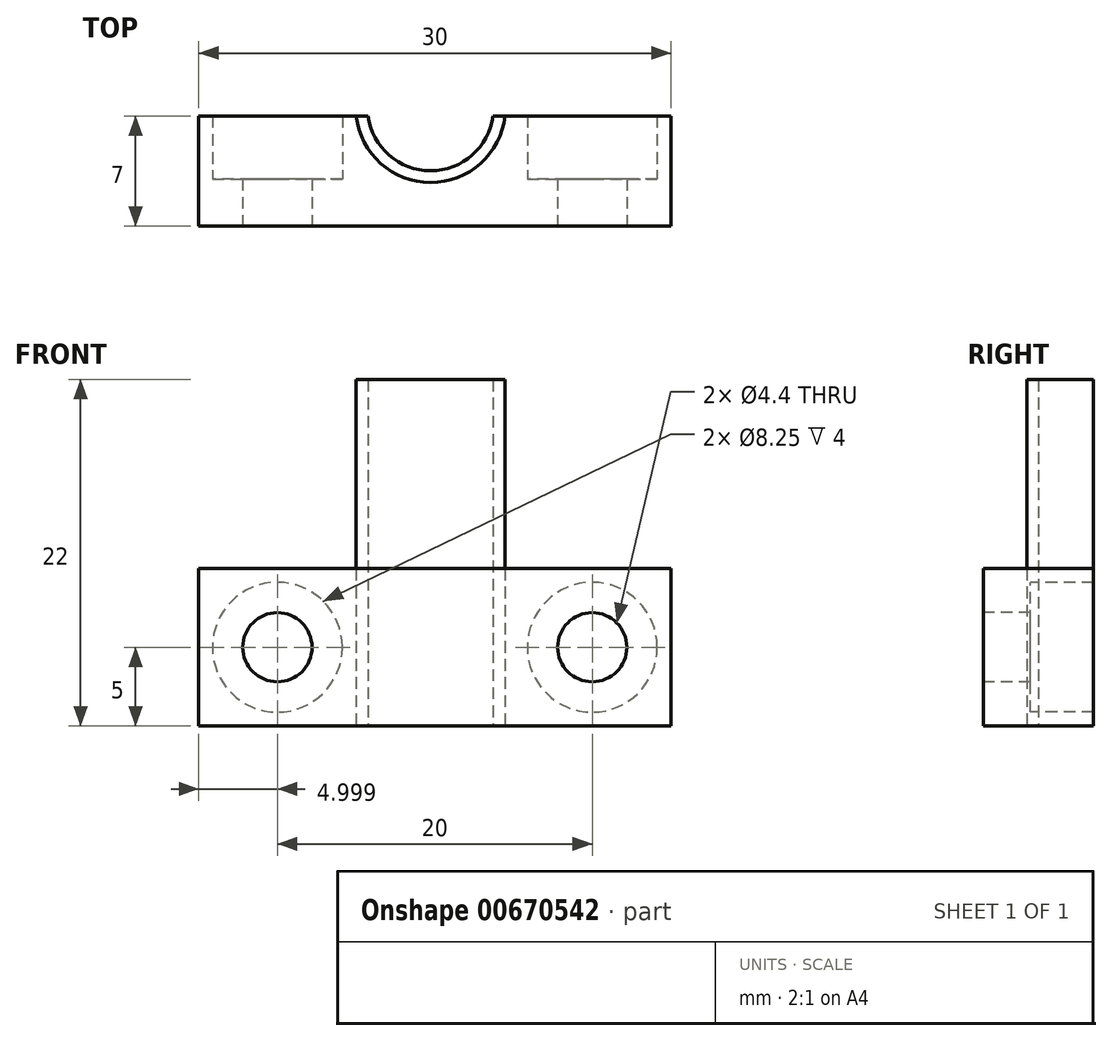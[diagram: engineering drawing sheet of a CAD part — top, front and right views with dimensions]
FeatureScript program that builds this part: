
annotation { "Feature Type Name" : "Feature", "Feature Type Description" : "" }
export const myFeature = defineFeature(function(context is Context, id is Id, definition is map)
    precondition{}
    {
        {
            var Q0;
            Q0=qCreatedBy(makeId("Top.planeOp"),FACE);
            var sketch = newSketch(context, id + "F0", { "sketchPlane" : qUnion([Q0])});
            skLineSegment(sketch, "E0", {"start": v(-9.42, 8.49) * mm, "end": v(10.65, 8.49) * mm});
            skPoint(sketch, "E1", {"position": v(0, 16) * mm});
            skArc(sketch, "E2", {"start": v(-3.97, 15.49) * mm, "mid": v(0, 12) * mm, "end": v(3.97, 15.49) * mm});
            skArc(sketch, "E3", {"start": v(-4.72, 15.49) * mm, "mid": v(0, 11.25) * mm, "end": v(4.72, 15.49) * mm});
            skLineSegment(sketch, "E4", {"start": v(-4.72, 15.49) * mm, "end": v(-3.97, 15.49) * mm});
            skLineSegment(sketch, "E5", {"start": v(4.72, 15.49) * mm, "end": v(3.97, 15.49) * mm});
            skLineSegment(sketch, "E6.trimOffspring", {"start": v(-3.97, 15.49) * mm, "end": v(-4.72, 15.49) * mm});
            skLineSegment(sketch, "E7", {"start": v(-4.72, 15.49) * mm, "end": v(-4.72, 8.49) * mm});
            skLineSegment(sketch, "E8", {"start": v(4.72, 15.49) * mm, "end": v(4.72, 8.49) * mm});
            skLineSegment(sketch, "E9", {"start": v(-4.72, 15.49) * mm, "end": v(-14.73, 15.49) * mm});
            skLineSegment(sketch, "E10", {"start": v(-14.73, 15.49) * mm, "end": v(-14.73, 8.49) * mm});
            skLineSegment(sketch, "E11", {"start": v(4.72, 15.49) * mm, "end": v(15.27, 15.49) * mm});
            skLineSegment(sketch, "E12", {"start": v(15.27, 15.49) * mm, "end": v(15.27, 8.49) * mm});
            skLineSegment(sketch, "E13", {"start": v(10.65, 8.49) * mm, "end": v(15.27, 8.49) * mm});
            skLineSegment(sketch, "E14", {"start": v(-9.42, 8.49) * mm, "end": v(-14.73, 8.49) * mm});
            skSolve(sketch);
        }
        {
            var Q0;
            Q0=makeQuery(id+"F0.imprint","IMPRINT",FACE,{"disambiguationData":[TD([[makeQuery(id+"F0.imprint","IMPRINT",EDGE,{"derivedFrom":sQuery(id+"F0.wireOp",EDGE,"E2")}),-1.0]])]});
            extrude(context, id + "F1", {"entities" : qUnion([Q0]), "depth" : 22 * mm, "offsetDistance" : 25 * mm, "flatOperationType" : FlatOperationType.REMOVE, "domain" : OperationDomain.MODEL});
        }
        {
            var Q0;
            {var subQ0=sQuery(id+"F0.wireOp",EDGE,"E7");var subQ1=sQuery(id+"F0.wireOp",EDGE,"E0");var subQ2=makeQuery(id+"F0.imprint","INTERSECT",VERTEX,{"derivedFrom":[subQ1,subQ0]});Q0=makeQuery(id+"F0.imprint","IMPRINT",FACE,{"disambiguationData":[TD([[makeQuery(id+"F0.imprint","IMPRINT",EDGE,{"disambiguationData":[TD([[subQ2,-1.0]])],"derivedFrom":subQ1}),1.0]])]});}
            var Q1;
            {var subQ0=sQuery(id+"F0.wireOp",EDGE,"E9");Q1=makeQuery(id+"F0.imprint","IMPRINT",FACE,{"disambiguationData":[TD([[makeQuery(id+"F0.imprint","IMPRINT",EDGE,{"derivedFrom":subQ0}),1.0]])]});}
            var Q2;
            {var subQ0=sQuery(id+"F0.wireOp",EDGE,"E12");Q2=makeQuery(id+"F0.imprint","IMPRINT",FACE,{"disambiguationData":[TD([[makeQuery(id+"F0.imprint","IMPRINT",EDGE,{"derivedFrom":subQ0}),-1.0]])]});}
            extrude(context, id + "F2", {"entities" : qUnion([Q0, Q1, Q2]), "depth" : 10 * mm, "offsetDistance" : 25 * mm, "flatOperationType" : FlatOperationType.REMOVE, "domain" : OperationDomain.MODEL});
        }
        {
            var Q0;
            Q0=makeQuery(id+"F2.opExtrude","SWEPT_FACE",FACE,{"disambiguationData":[OSD([sQuery(id+"F0.wireOp",EDGE,"E11")])]});
            var sketch = newSketch(context, id + "F3", { "sketchPlane" : qUnion([Q0])});
            skPoint(sketch, "E15", {"position": v(-10.27, 5) * mm});
            skPoint(sketch, "E16", {"position": v(9.73, 5) * mm});
            skSolve(sketch);
        }
        {
            var Q0;
            Q0=sQuery(id+"F3.wireOp",VERTEX,"E15");
            var Q1;
            Q1=sQuery(id+"F3.wireOp",VERTEX,"E16");
            var Q2;
            Q2=makeQuery(id+"FKl3BDI6fezDzpM_0.opExtrude","SWEPT_BODY",BODY,{"disambiguationData":[OSD([sQuery(id+"F0.wireOp",EDGE,"fsfPvmrl-390t-10xi-3nHy-8umhwFnufOJv.top"),sQuery(id+"F0.wireOp",EDGE,"fsfPvmrl-390t-10xi-3nHy-8umhwFnufOJv.left"),sQuery(id+"F0.wireOp",EDGE,"fsfPvmrl-390t-10xi-3nHy-8umhwFnufOJv.right"),sQuery(id+"F0.wireOp",EDGE,"CcvFbTlt-zD4W-8NPh-LdsS-PvNdjG0tOvnu"),sQuery(id+"F0.wireOp",EDGE,"pVby3J4y-x7wc-o6gS-JqxG-tS4zD72zG29G"),sQuery(id+"F0.wireOp",EDGE,"E0"),sQuery(id+"F0.wireOp",EDGE,"FWo3jG2l-GR7Q-KomG-45ht-qYG2UUJcV63A.bottom"),sQuery(id+"F0.wireOp",EDGE,"GzCtnEaw-SK8U-iIZo-P1jO-m6GxNIaJTrVv.top")])]});
            var Q3;
            Q3=makeQuery(id+"F2.opExtrude","SWEPT_BODY",BODY,{"disambiguationData":[OSD([sQuery(id+"F0.wireOp",EDGE,"CcvFbTlt-zD4W-8NPh-LdsS-PvNdjG0tOvnu"),sQuery(id+"F0.wireOp",EDGE,"pVby3J4y-x7wc-o6gS-JqxG-tS4zD72zG29G"),sQuery(id+"F0.wireOp",EDGE,"E0"),sQuery(id+"F0.wireOp",EDGE,"E3"),sQuery(id+"F0.wireOp",EDGE,"E7"),sQuery(id+"F0.wireOp",EDGE,"E9"),sQuery(id+"F0.wireOp",EDGE,"E10"),sQuery(id+"F0.wireOp",EDGE,"E11"),sQuery(id+"F0.wireOp",EDGE,"E12")])]});
            hole(context, id + "F4", {"style" : HoleStyle.C_BORE, "endStyle" : HoleEndStyle.BLIND, "holeDiameter" : 4.4 * mm, "cBoreDiameter" : 8.25 * mm, "cBoreDepth" : 4 * mm, "majorDiameter" : 4 * mm, "holeDepth" : 8 * mm, "tappedDepth" : 15 * mm, "tapClearance" : 0, "locations" : qUnion([Q0, Q1]), "scope" : qUnion([Q2, Q3]), "startStyle" : HoleStartStyle.PART});
        }
    });
